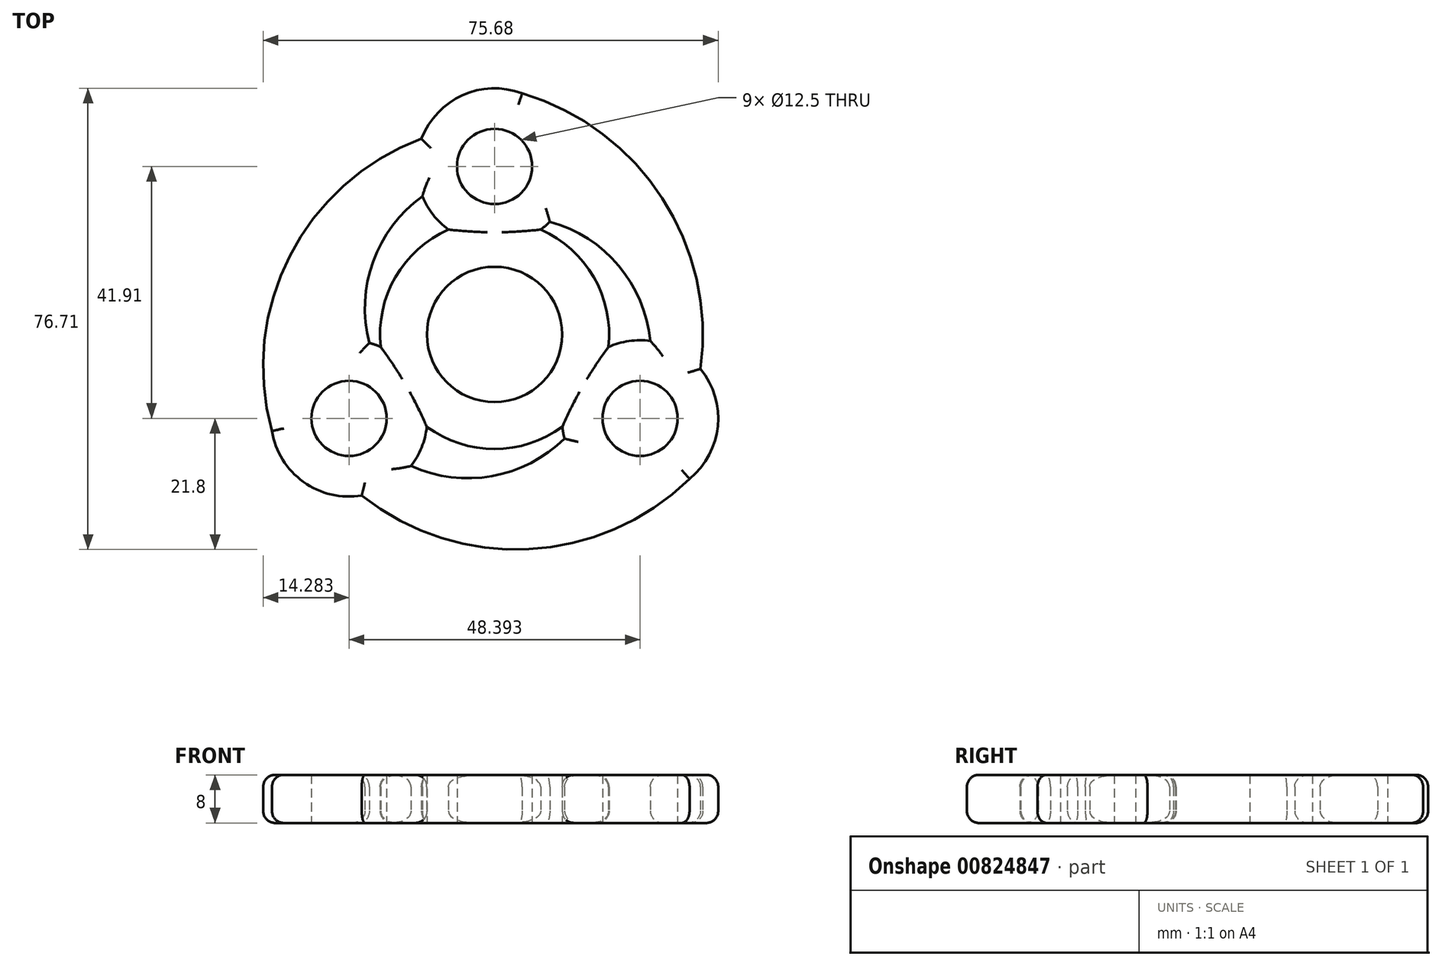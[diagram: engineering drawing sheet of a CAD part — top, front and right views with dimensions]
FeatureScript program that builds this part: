
annotation { "Feature Type Name" : "Feature", "Feature Type Description" : "" }
export const myFeature = defineFeature(function(context is Context, id is Id, definition is map)
    precondition{}
    {
        {
            var Q0;
            Q0=qCreatedBy(makeId("Top.planeOp"),FACE);
            var sketch = newSketch(context, id + "F0", { "sketchPlane" : qUnion([Q0])});
            skCircle(sketch, "E0", {"center": v(0, 0) * mm, "radius": 11.25 * mm});
            skCircle(sketch, "E1", {"center": v(0, 0) * mm, "radius": 19.05 * mm});
            skCircle(sketch, "E2", {"center": v(0, 27.94) * mm, "radius": 6.25 * mm});
            skCircle(sketch, "E3", {"center": v(0, 27.94) * mm, "radius": 13 * mm});
            skCircle(sketch, "E4", {"center": v(0, 0) * mm, "radius": 40.94 * mm, "construction": true});
            skLineSegment(sketch, "E5", {"start": v(-13, 27.94) * mm, "end": v(13, 27.94) * mm, "construction": true});
            skLineSegment(sketch, "E6", {"start": v(0, 27.94) * mm, "end": v(9.2, 37.13) * mm, "construction": true});
            skLineSegment(sketch, "E7", {"start": v(0, 27.94) * mm, "end": v(4.6, 40.1) * mm, "construction": true});
            skPoint(sketch, "E7.endSnap0", {"position": v(4.6, 39.04) * mm});
            skLineSegment(sketch, "E8", {"start": v(0, 27.94) * mm, "end": v(12.01, 32.91) * mm, "construction": true});
            skLineSegment(sketch, "E9", {"start": v(0, 27.94) * mm, "end": v(9.2, 18.75) * mm, "construction": true});
            skLineSegment(sketch, "E10", {"start": v(0, 27.94) * mm, "end": v(12.16, 23.34) * mm, "construction": true});
            skLineSegment(sketch, "E11", {"start": v(0, 27.94) * mm, "end": v(4.97, 15.93) * mm, "construction": true});
            skLineSegment(sketch, "E12", {"start": v(0, 27.94) * mm, "end": v(-9.2, 18.75) * mm, "construction": true});
            skLineSegment(sketch, "E13", {"start": v(0, 27.94) * mm, "end": v(-4.6, 15.78) * mm, "construction": true});
            skLineSegment(sketch, "E14", {"start": v(0, 27.94) * mm, "end": v(-12.01, 22.97) * mm, "construction": true});
            skLineSegment(sketch, "E15", {"start": v(0, 27.94) * mm, "end": v(-9.2, 37.13) * mm, "construction": true});
            skLineSegment(sketch, "E16", {"start": v(0, 27.94) * mm, "end": v(-12.16, 32.54) * mm, "construction": true});
            skLineSegment(sketch, "E17", {"start": v(0, 27.94) * mm, "end": v(-4.97, 39.95) * mm, "construction": true});
            skLineSegment(sketch, "E18", {"start": v(0, 14.94) * mm, "end": v(0, 40.94) * mm, "construction": true});
            skLineSegment(sketch, "E19.1.0", {"start": v(-24.2, -13.97) * mm, "end": v(-22.1, -26.8) * mm, "construction": true});
            skLineSegment(sketch, "E19.1.1", {"start": v(-24.2, -13.97) * mm, "end": v(-13.88, -21.88) * mm, "construction": true});
            skLineSegment(sketch, "E19.1.2", {"start": v(-24.2, -13.97) * mm, "end": v(-26.3, -1.14) * mm, "construction": true});
            skCircle(sketch, "E19.1.3", {"center": v(-24.2, -13.97) * mm, "radius": 6.25 * mm});
            skLineSegment(sketch, "E19.1.4", {"start": v(-17.7, -25.23) * mm, "end": v(-30.7, -2.71) * mm, "construction": true});
            skLineSegment(sketch, "E19.1.5", {"start": v(-24.2, -13.97) * mm, "end": v(-34.51, -6.06) * mm, "construction": true});
            skLineSegment(sketch, "E19.1.6", {"start": v(-24.2, -13.97) * mm, "end": v(-20.83, -1.41) * mm, "construction": true});
            skLineSegment(sketch, "E19.1.7", {"start": v(-24.2, -13.97) * mm, "end": v(-16.28, -3.66) * mm, "construction": true});
            skLineSegment(sketch, "E19.1.8", {"start": v(-12.94, -7.47) * mm, "end": v(-35.46, -20.47) * mm, "construction": true});
            skLineSegment(sketch, "E19.1.9", {"start": v(-24.2, -13.97) * mm, "end": v(-11.37, -11.87) * mm, "construction": true});
            skLineSegment(sketch, "E19.1.10", {"start": v(-24.2, -13.97) * mm, "end": v(-11.64, -17.33) * mm, "construction": true});
            skLineSegment(sketch, "E19.1.11", {"start": v(-24.2, -13.97) * mm, "end": v(-27.56, -26.53) * mm, "construction": true});
            skLineSegment(sketch, "E19.1.12", {"start": v(-24.2, -13.97) * mm, "end": v(-32.11, -24.28) * mm, "construction": true});
            skLineSegment(sketch, "E19.1.13", {"start": v(-24.2, -13.97) * mm, "end": v(-37.03, -16.07) * mm, "construction": true});
            skLineSegment(sketch, "E19.1.14", {"start": v(-24.2, -13.97) * mm, "end": v(-36.75, -10.6) * mm, "construction": true});
            skCircle(sketch, "E19.1.15", {"center": v(-24.2, -13.97) * mm, "radius": 13 * mm});
            skLineSegment(sketch, "E19.2.0", {"start": v(24.2, -13.97) * mm, "end": v(34.26, -5.74) * mm, "construction": true});
            skLineSegment(sketch, "E19.2.1", {"start": v(24.2, -13.97) * mm, "end": v(25.9, -1.08) * mm, "construction": true});
            skLineSegment(sketch, "E19.2.2", {"start": v(24.2, -13.97) * mm, "end": v(14.14, -22.2) * mm, "construction": true});
            skCircle(sketch, "E19.2.3", {"center": v(24.2, -13.97) * mm, "radius": 6.25 * mm});
            skLineSegment(sketch, "E19.2.4", {"start": v(30.7, -2.71) * mm, "end": v(17.7, -25.23) * mm, "construction": true});
            skLineSegment(sketch, "E19.2.5", {"start": v(24.2, -13.97) * mm, "end": v(22.5, -26.86) * mm, "construction": true});
            skLineSegment(sketch, "E19.2.6", {"start": v(24.2, -13.97) * mm, "end": v(11.64, -17.33) * mm, "construction": true});
            skLineSegment(sketch, "E19.2.7", {"start": v(24.2, -13.97) * mm, "end": v(11.3, -12.27) * mm, "construction": true});
            skLineSegment(sketch, "E19.2.8", {"start": v(12.94, -7.47) * mm, "end": v(35.46, -20.47) * mm, "construction": true});
            skLineSegment(sketch, "E19.2.9", {"start": v(24.2, -13.97) * mm, "end": v(15.96, -3.9) * mm, "construction": true});
            skLineSegment(sketch, "E19.2.10", {"start": v(24.2, -13.97) * mm, "end": v(20.83, -1.41) * mm, "construction": true});
            skLineSegment(sketch, "E19.2.11", {"start": v(24.2, -13.97) * mm, "end": v(36.75, -10.6) * mm, "construction": true});
            skLineSegment(sketch, "E19.2.12", {"start": v(24.2, -13.97) * mm, "end": v(37.09, -15.67) * mm, "construction": true});
            skLineSegment(sketch, "E19.2.13", {"start": v(24.2, -13.97) * mm, "end": v(32.43, -24.03) * mm, "construction": true});
            skLineSegment(sketch, "E19.2.14", {"start": v(24.2, -13.97) * mm, "end": v(27.56, -26.53) * mm, "construction": true});
            skCircle(sketch, "E19.2.15", {"center": v(24.2, -13.97) * mm, "radius": 13 * mm});
            skArc(sketch, "E20", {"start": v(34.26, -5.74) * mm, "mid": v(27.9, 22.67) * mm, "end": v(4.6, 40.1) * mm});
            skArc(sketch, "E21", {"start": v(-22.1, -26.8) * mm, "mid": v(5.69, -35.72) * mm, "end": v(32.43, -24.03) * mm});
            skArc(sketch, "E22", {"start": v(-12.16, 32.54) * mm, "mid": v(-34.05, 13.07) * mm, "end": v(-37.03, -16.07) * mm});
            skArc(sketch, "E23", {"start": v(-12.01, 22.97) * mm, "mid": v(-20.2, 12.14) * mm, "end": v(-20.83, -1.41) * mm});
            skArc(sketch, "E24", {"start": v(25.9, -1.08) * mm, "mid": v(20.63, 11.43) * mm, "end": v(9.2, 18.75) * mm});
            skArc(sketch, "E25", {"start": v(-13.88, -21.88) * mm, "mid": v(-0.42, -23.57) * mm, "end": v(11.64, -17.33) * mm});
            skSolve(sketch);
        }
        {
            var Q0;
            {var subQ0=sQuery(id+"F0.wireOp",EDGE,"E22");Q0=makeQuery(id+"F0.imprint","IMPRINT",FACE,{"disambiguationData":[TD([[makeQuery(id+"F0.imprint","IMPRINT",EDGE,{"derivedFrom":subQ0}),1.0]])]});}
            var Q1;
            {var subQ0=sQuery(id+"F0.wireOp",EDGE,"E20");Q1=makeQuery(id+"F0.imprint","IMPRINT",FACE,{"disambiguationData":[TD([[makeQuery(id+"F0.imprint","IMPRINT",EDGE,{"derivedFrom":subQ0}),1.0]])]});}
            var Q2;
            {var subQ0=sQuery(id+"F0.wireOp",EDGE,"E21");Q2=makeQuery(id+"F0.imprint","IMPRINT",FACE,{"disambiguationData":[TD([[makeQuery(id+"F0.imprint","IMPRINT",EDGE,{"derivedFrom":subQ0}),1.0]])]});}
            var Q3;
            Q3=makeQuery(id+"F0.imprint","IMPRINT",FACE,{"disambiguationData":[TD([[makeQuery(id+"F0.imprint","IMPRINT",EDGE,{"derivedFrom":sQuery(id+"F0.wireOp",EDGE,"E19.2.3")}),-1.0]])]});
            var Q4;
            {var subQ0=sQuery(id+"F0.wireOp",EDGE,"E19.2.15");var subQ1=sQuery(id+"F0.wireOp",EDGE,"E1");var subQ2=makeQuery(id+"F0.imprint","INTERSECT",VERTEX,{"disambiguationData":[OD(0.0)],"derivedFrom":[subQ1,subQ0]});Q4=makeQuery(id+"F0.imprint","IMPRINT",FACE,{"disambiguationData":[TD([[makeQuery(id+"F0.imprint","IMPRINT",EDGE,{"disambiguationData":[TD([[subQ2,-1.0]])],"derivedFrom":subQ1}),1.0]])]});}
            var Q5;
            Q5=makeQuery(id+"F0.imprint","IMPRINT",FACE,{"disambiguationData":[TD([[makeQuery(id+"F0.imprint","IMPRINT",EDGE,{"derivedFrom":sQuery(id+"F0.wireOp",EDGE,"E0")}),-1.0]])]});
            var Q6;
            {var subQ0=sQuery(id+"F0.wireOp",EDGE,"E19.1.15");var subQ1=sQuery(id+"F0.wireOp",EDGE,"E1");var subQ2=makeQuery(id+"F0.imprint","INTERSECT",VERTEX,{"disambiguationData":[OD(0.0)],"derivedFrom":[subQ1,subQ0]});Q6=makeQuery(id+"F0.imprint","IMPRINT",FACE,{"disambiguationData":[TD([[makeQuery(id+"F0.imprint","IMPRINT",EDGE,{"disambiguationData":[TD([[subQ2,-1.0]])],"derivedFrom":subQ1}),1.0]])]});}
            var Q7;
            Q7=makeQuery(id+"F0.imprint","IMPRINT",FACE,{"disambiguationData":[TD([[makeQuery(id+"F0.imprint","IMPRINT",EDGE,{"derivedFrom":sQuery(id+"F0.wireOp",EDGE,"E19.1.3")}),-1.0]])]});
            var Q8;
            Q8=makeQuery(id+"F0.imprint","IMPRINT",FACE,{"disambiguationData":[TD([[makeQuery(id+"F0.imprint","IMPRINT",EDGE,{"derivedFrom":sQuery(id+"F0.wireOp",EDGE,"E2")}),-1.0]])]});
            var Q9;
            {var subQ0=sQuery(id+"F0.wireOp",EDGE,"E3");var subQ1=sQuery(id+"F0.wireOp",EDGE,"E1");var subQ2=makeQuery(id+"F0.imprint","INTERSECT",VERTEX,{"disambiguationData":[OD(0.0)],"derivedFrom":[subQ1,subQ0]});Q9=makeQuery(id+"F0.imprint","IMPRINT",FACE,{"disambiguationData":[TD([[makeQuery(id+"F0.imprint","IMPRINT",EDGE,{"disambiguationData":[TD([[subQ2,1.0]])],"derivedFrom":subQ1}),1.0]])]});}
            extrude(context, id + "F1", {"entities" : qUnion([Q0, Q1, Q2, Q3, Q4, Q5, Q6, Q7, Q8, Q9]), "depth" : 8 * mm, "offsetDistance" : 25 * mm});
        }
        {
            var Q0;
            Q0=makeQuery(id+"F1.opExtrude","CAP_EDGE",EDGE,{"disambiguationData":[OSD([sQuery(id+"F0.wireOp",EDGE,"E22")])],"isStart":false});
            var Q1;
            {var subQ0=sQuery(id+"F0.wireOp",EDGE,"E3");Q1=makeQuery(id+"F1.opExtrude","CAP_EDGE",EDGE,{"disambiguationData":[OSD([subQ0]),TDD([makeQuery(id+"F0.imprint","IMPRINT",EDGE,{"disambiguationData":[TD([[makeQuery(id+"F0.imprint","INTERSECT",VERTEX,{"derivedFrom":[subQ0,sQuery(id+"F0.wireOp",EDGE,"E20")]}),-1.0]])],"derivedFrom":subQ0})])],"isStart":false});}
            var Q2;
            Q2=makeQuery(id+"F1.opExtrude","CAP_EDGE",EDGE,{"disambiguationData":[OSD([sQuery(id+"F0.wireOp",EDGE,"E20")])],"isStart":false});
            var Q3;
            {var subQ0=sQuery(id+"F0.wireOp",EDGE,"E19.2.15");Q3=makeQuery(id+"F1.opExtrude","CAP_EDGE",EDGE,{"disambiguationData":[OSD([subQ0]),TDD([makeQuery(id+"F0.imprint","IMPRINT",EDGE,{"disambiguationData":[TD([[makeQuery(id+"F0.imprint","INTERSECT",VERTEX,{"derivedFrom":[subQ0,sQuery(id+"F0.wireOp",EDGE,"E20")]}),1.0]])],"derivedFrom":subQ0})])],"isStart":false});}
            var Q4;
            Q4=makeQuery(id+"F1.opExtrude","CAP_EDGE",EDGE,{"disambiguationData":[OSD([sQuery(id+"F0.wireOp",EDGE,"E21")])],"isStart":false});
            var Q5;
            {var subQ0=sQuery(id+"F0.wireOp",EDGE,"E19.1.15");Q5=makeQuery(id+"F1.opExtrude","CAP_EDGE",EDGE,{"disambiguationData":[OSD([subQ0]),TDD([makeQuery(id+"F0.imprint","IMPRINT",EDGE,{"disambiguationData":[TD([[makeQuery(id+"F0.imprint","INTERSECT",VERTEX,{"derivedFrom":[subQ0,sQuery(id+"F0.wireOp",EDGE,"E21")]}),1.0]])],"derivedFrom":subQ0})])],"isStart":false});}
            var Q6;
            {var subQ0=sQuery(id+"F0.wireOp",EDGE,"E19.1.15");Q6=makeQuery(id+"F1.opExtrude","CAP_EDGE",EDGE,{"disambiguationData":[OSD([subQ0]),TDD([makeQuery(id+"F0.imprint","IMPRINT",EDGE,{"disambiguationData":[TD([[makeQuery(id+"F0.imprint","INTERSECT",VERTEX,{"derivedFrom":[subQ0,sQuery(id+"F0.wireOp",EDGE,"E25")]}),-1.0]])],"derivedFrom":subQ0})])],"isStart":false});}
            var Q7;
            {var subQ0=sQuery(id+"F0.wireOp",EDGE,"E1");Q7=makeQuery(id+"F1.opExtrude","CAP_EDGE",EDGE,{"disambiguationData":[OSD([subQ0]),TDD([makeQuery(id+"F0.imprint","IMPRINT",EDGE,{"disambiguationData":[TD([[makeQuery(id+"F0.imprint","INTERSECT",VERTEX,{"disambiguationData":[OD(1.0)],"derivedFrom":[subQ0,sQuery(id+"F0.wireOp",EDGE,"E19.1.15")]}),-1.0]])],"derivedFrom":subQ0})])],"isStart":false});}
            var Q8;
            Q8=makeQuery(id+"F1.opExtrude","CAP_EDGE",EDGE,{"disambiguationData":[OSD([sQuery(id+"F0.wireOp",EDGE,"E25")])],"isStart":false});
            var Q9;
            {var subQ0=sQuery(id+"F0.wireOp",EDGE,"E19.2.15");Q9=makeQuery(id+"F1.opExtrude","CAP_EDGE",EDGE,{"disambiguationData":[OSD([subQ0]),TDD([makeQuery(id+"F0.imprint","IMPRINT",EDGE,{"disambiguationData":[TD([[makeQuery(id+"F0.imprint","INTERSECT",VERTEX,{"derivedFrom":[subQ0,sQuery(id+"F0.wireOp",EDGE,"E25")]}),1.0]])],"derivedFrom":subQ0})])],"isStart":false});}
            var Q10;
            {var subQ0=sQuery(id+"F0.wireOp",EDGE,"E1");Q10=makeQuery(id+"F1.opExtrude","CAP_EDGE",EDGE,{"disambiguationData":[OSD([subQ0]),TDD([makeQuery(id+"F0.imprint","IMPRINT",EDGE,{"disambiguationData":[TD([[makeQuery(id+"F0.imprint","INTERSECT",VERTEX,{"disambiguationData":[OD(1.0)],"derivedFrom":[subQ0,sQuery(id+"F0.wireOp",EDGE,"E3")]}),1.0]])],"derivedFrom":subQ0})])],"isStart":false});}
            var Q11;
            Q11=makeQuery(id+"F1.opExtrude","CAP_EDGE",EDGE,{"disambiguationData":[OSD([sQuery(id+"F0.wireOp",EDGE,"E24")])],"isStart":false});
            var Q12;
            {var subQ0=sQuery(id+"F0.wireOp",EDGE,"E19.2.15");Q12=makeQuery(id+"F1.opExtrude","CAP_EDGE",EDGE,{"disambiguationData":[OSD([subQ0]),TDD([makeQuery(id+"F0.imprint","IMPRINT",EDGE,{"disambiguationData":[TD([[makeQuery(id+"F0.imprint","INTERSECT",VERTEX,{"derivedFrom":[subQ0,sQuery(id+"F0.wireOp",EDGE,"E24")]}),-1.0]])],"derivedFrom":subQ0})])],"isStart":false});}
            var Q13;
            {var subQ0=sQuery(id+"F0.wireOp",EDGE,"E3");Q13=makeQuery(id+"F1.opExtrude","CAP_EDGE",EDGE,{"disambiguationData":[OSD([subQ0]),TDD([makeQuery(id+"F0.imprint","IMPRINT",EDGE,{"disambiguationData":[TD([[makeQuery(id+"F0.imprint","INTERSECT",VERTEX,{"derivedFrom":[subQ0,sQuery(id+"F0.wireOp",EDGE,"E24")]}),1.0]])],"derivedFrom":subQ0})])],"isStart":false});}
            var Q14;
            {var subQ0=sQuery(id+"F0.wireOp",EDGE,"E1");Q14=makeQuery(id+"F1.opExtrude","CAP_EDGE",EDGE,{"disambiguationData":[OSD([subQ0]),TDD([makeQuery(id+"F0.imprint","IMPRINT",EDGE,{"disambiguationData":[TD([[makeQuery(id+"F0.imprint","INTERSECT",VERTEX,{"disambiguationData":[OD(0.0)],"derivedFrom":[subQ0,sQuery(id+"F0.wireOp",EDGE,"E3")]}),-1.0]])],"derivedFrom":subQ0})])],"isStart":false});}
            var Q15;
            {var subQ0=sQuery(id+"F0.wireOp",EDGE,"E19.1.15");Q15=makeQuery(id+"F1.opExtrude","CAP_EDGE",EDGE,{"disambiguationData":[OSD([subQ0]),TDD([makeQuery(id+"F0.imprint","IMPRINT",EDGE,{"disambiguationData":[TD([[makeQuery(id+"F0.imprint","INTERSECT",VERTEX,{"derivedFrom":[subQ0,sQuery(id+"F0.wireOp",EDGE,"E23")]}),1.0]])],"derivedFrom":subQ0})])],"isStart":false});}
            var Q16;
            Q16=makeQuery(id+"F1.opExtrude","CAP_EDGE",EDGE,{"disambiguationData":[OSD([sQuery(id+"F0.wireOp",EDGE,"E23")])],"isStart":false});
            var Q17;
            {var subQ0=sQuery(id+"F0.wireOp",EDGE,"E3");Q17=makeQuery(id+"F1.opExtrude","CAP_EDGE",EDGE,{"disambiguationData":[OSD([subQ0]),TDD([makeQuery(id+"F0.imprint","IMPRINT",EDGE,{"disambiguationData":[TD([[makeQuery(id+"F0.imprint","INTERSECT",VERTEX,{"derivedFrom":[subQ0,sQuery(id+"F0.wireOp",EDGE,"E23")]}),-1.0]])],"derivedFrom":subQ0})])],"isStart":false});}
            fillet(context, id + "F2", {"entities" : qUnion([Q0, Q1, Q2, Q3, Q4, Q5, Q6, Q7, Q8, Q9, Q10, Q11, Q12, Q13, Q14, Q15, Q16, Q17]), "radius" : 2 * mm, "tangentPropagation" : true, "allowEdgeOverflow" : false});
        }
        {
            var Q0;
            Q0=makeQuery(id+"F1.opExtrude","CAP_EDGE",EDGE,{"disambiguationData":[OSD([sQuery(id+"F0.wireOp",EDGE,"E22")])],"isStart":true});
            var Q1;
            {var subQ0=sQuery(id+"F0.wireOp",EDGE,"E3");Q1=makeQuery(id+"F1.opExtrude","CAP_EDGE",EDGE,{"disambiguationData":[OSD([subQ0]),TDD([makeQuery(id+"F0.imprint","IMPRINT",EDGE,{"disambiguationData":[TD([[makeQuery(id+"F0.imprint","INTERSECT",VERTEX,{"derivedFrom":[subQ0,sQuery(id+"F0.wireOp",EDGE,"E20")]}),-1.0]])],"derivedFrom":subQ0})])],"isStart":true});}
            var Q2;
            Q2=makeQuery(id+"F1.opExtrude","CAP_EDGE",EDGE,{"disambiguationData":[OSD([sQuery(id+"F0.wireOp",EDGE,"E20")])],"isStart":true});
            var Q3;
            {var subQ0=sQuery(id+"F0.wireOp",EDGE,"E19.2.15");Q3=makeQuery(id+"F1.opExtrude","CAP_EDGE",EDGE,{"disambiguationData":[OSD([subQ0]),TDD([makeQuery(id+"F0.imprint","IMPRINT",EDGE,{"disambiguationData":[TD([[makeQuery(id+"F0.imprint","INTERSECT",VERTEX,{"derivedFrom":[subQ0,sQuery(id+"F0.wireOp",EDGE,"E20")]}),1.0]])],"derivedFrom":subQ0})])],"isStart":true});}
            var Q4;
            Q4=makeQuery(id+"F1.opExtrude","CAP_EDGE",EDGE,{"disambiguationData":[OSD([sQuery(id+"F0.wireOp",EDGE,"E21")])],"isStart":true});
            var Q5;
            {var subQ0=sQuery(id+"F0.wireOp",EDGE,"E19.1.15");Q5=makeQuery(id+"F1.opExtrude","CAP_EDGE",EDGE,{"disambiguationData":[OSD([subQ0]),TDD([makeQuery(id+"F0.imprint","IMPRINT",EDGE,{"disambiguationData":[TD([[makeQuery(id+"F0.imprint","INTERSECT",VERTEX,{"derivedFrom":[subQ0,sQuery(id+"F0.wireOp",EDGE,"E21")]}),1.0]])],"derivedFrom":subQ0})])],"isStart":true});}
            var Q6;
            Q6=makeQuery(id+"F1.opExtrude","CAP_EDGE",EDGE,{"disambiguationData":[OSD([sQuery(id+"F0.wireOp",EDGE,"E23")])],"isStart":true});
            var Q7;
            {var subQ0=sQuery(id+"F0.wireOp",EDGE,"E1");Q7=makeQuery(id+"F1.opExtrude","CAP_EDGE",EDGE,{"disambiguationData":[OSD([subQ0]),TDD([makeQuery(id+"F0.imprint","IMPRINT",EDGE,{"disambiguationData":[TD([[makeQuery(id+"F0.imprint","INTERSECT",VERTEX,{"disambiguationData":[OD(0.0)],"derivedFrom":[subQ0,sQuery(id+"F0.wireOp",EDGE,"E3")]}),-1.0]])],"derivedFrom":subQ0})])],"isStart":true});}
            var Q8;
            {var subQ0=sQuery(id+"F0.wireOp",EDGE,"E19.1.15");Q8=makeQuery(id+"F1.opExtrude","CAP_EDGE",EDGE,{"disambiguationData":[OSD([subQ0]),TDD([makeQuery(id+"F0.imprint","IMPRINT",EDGE,{"disambiguationData":[TD([[makeQuery(id+"F0.imprint","INTERSECT",VERTEX,{"derivedFrom":[subQ0,sQuery(id+"F0.wireOp",EDGE,"E23")]}),1.0]])],"derivedFrom":subQ0})])],"isStart":true});}
            var Q9;
            {var subQ0=sQuery(id+"F0.wireOp",EDGE,"E19.1.15");Q9=makeQuery(id+"F1.opExtrude","CAP_EDGE",EDGE,{"disambiguationData":[OSD([subQ0]),TDD([makeQuery(id+"F0.imprint","IMPRINT",EDGE,{"disambiguationData":[TD([[makeQuery(id+"F0.imprint","INTERSECT",VERTEX,{"derivedFrom":[subQ0,sQuery(id+"F0.wireOp",EDGE,"E25")]}),-1.0]])],"derivedFrom":subQ0})])],"isStart":true});}
            var Q10;
            Q10=makeQuery(id+"F1.opExtrude","CAP_EDGE",EDGE,{"disambiguationData":[OSD([sQuery(id+"F0.wireOp",EDGE,"E25")])],"isStart":true});
            var Q11;
            {var subQ0=sQuery(id+"F0.wireOp",EDGE,"E1");Q11=makeQuery(id+"F1.opExtrude","CAP_EDGE",EDGE,{"disambiguationData":[OSD([subQ0]),TDD([makeQuery(id+"F0.imprint","IMPRINT",EDGE,{"disambiguationData":[TD([[makeQuery(id+"F0.imprint","INTERSECT",VERTEX,{"disambiguationData":[OD(1.0)],"derivedFrom":[subQ0,sQuery(id+"F0.wireOp",EDGE,"E19.1.15")]}),-1.0]])],"derivedFrom":subQ0})])],"isStart":true});}
            var Q12;
            {var subQ0=sQuery(id+"F0.wireOp",EDGE,"E19.2.15");Q12=makeQuery(id+"F1.opExtrude","CAP_EDGE",EDGE,{"disambiguationData":[OSD([subQ0]),TDD([makeQuery(id+"F0.imprint","IMPRINT",EDGE,{"disambiguationData":[TD([[makeQuery(id+"F0.imprint","INTERSECT",VERTEX,{"derivedFrom":[subQ0,sQuery(id+"F0.wireOp",EDGE,"E25")]}),1.0]])],"derivedFrom":subQ0})])],"isStart":true});}
            var Q13;
            {var subQ0=sQuery(id+"F0.wireOp",EDGE,"E1");Q13=makeQuery(id+"F1.opExtrude","CAP_EDGE",EDGE,{"disambiguationData":[OSD([subQ0]),TDD([makeQuery(id+"F0.imprint","IMPRINT",EDGE,{"disambiguationData":[TD([[makeQuery(id+"F0.imprint","INTERSECT",VERTEX,{"disambiguationData":[OD(1.0)],"derivedFrom":[subQ0,sQuery(id+"F0.wireOp",EDGE,"E3")]}),1.0]])],"derivedFrom":subQ0})])],"isStart":true});}
            var Q14;
            Q14=makeQuery(id+"F1.opExtrude","CAP_EDGE",EDGE,{"disambiguationData":[OSD([sQuery(id+"F0.wireOp",EDGE,"E24")])],"isStart":true});
            var Q15;
            {var subQ0=sQuery(id+"F0.wireOp",EDGE,"E19.2.15");Q15=makeQuery(id+"F1.opExtrude","CAP_EDGE",EDGE,{"disambiguationData":[OSD([subQ0]),TDD([makeQuery(id+"F0.imprint","IMPRINT",EDGE,{"disambiguationData":[TD([[makeQuery(id+"F0.imprint","INTERSECT",VERTEX,{"derivedFrom":[subQ0,sQuery(id+"F0.wireOp",EDGE,"E24")]}),-1.0]])],"derivedFrom":subQ0})])],"isStart":true});}
            var Q16;
            {var subQ0=sQuery(id+"F0.wireOp",EDGE,"E3");Q16=makeQuery(id+"F1.opExtrude","CAP_EDGE",EDGE,{"disambiguationData":[OSD([subQ0]),TDD([makeQuery(id+"F0.imprint","IMPRINT",EDGE,{"disambiguationData":[TD([[makeQuery(id+"F0.imprint","INTERSECT",VERTEX,{"derivedFrom":[subQ0,sQuery(id+"F0.wireOp",EDGE,"E24")]}),1.0]])],"derivedFrom":subQ0})])],"isStart":true});}
            var Q17;
            {var subQ0=sQuery(id+"F0.wireOp",EDGE,"E3");Q17=makeQuery(id+"F1.opExtrude","CAP_EDGE",EDGE,{"disambiguationData":[OSD([subQ0]),TDD([makeQuery(id+"F0.imprint","IMPRINT",EDGE,{"disambiguationData":[TD([[makeQuery(id+"F0.imprint","INTERSECT",VERTEX,{"derivedFrom":[subQ0,sQuery(id+"F0.wireOp",EDGE,"E23")]}),-1.0]])],"derivedFrom":subQ0})])],"isStart":true});}
            fillet(context, id + "F3", {"entities" : qUnion([Q0, Q1, Q2, Q3, Q4, Q5, Q6, Q7, Q8, Q9, Q10, Q11, Q12, Q13, Q14, Q15, Q16, Q17]), "radius" : 2 * mm, "tangentPropagation" : true, "allowEdgeOverflow" : false});
        }
    });
